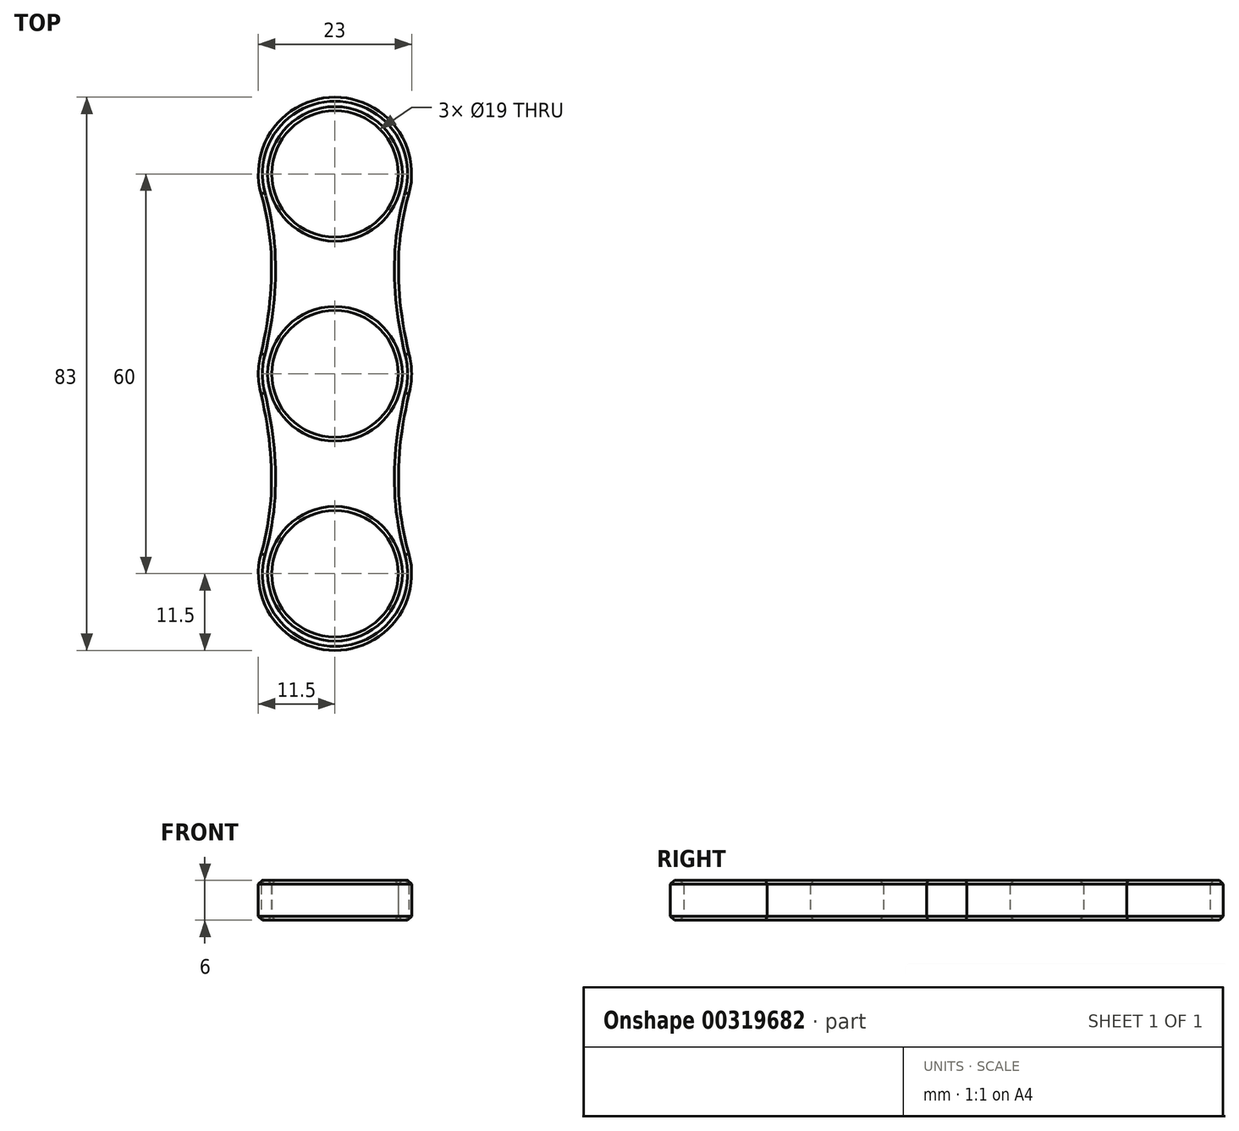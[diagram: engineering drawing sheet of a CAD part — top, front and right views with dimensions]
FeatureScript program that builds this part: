
annotation { "Feature Type Name" : "Feature", "Feature Type Description" : "" }
export const myFeature = defineFeature(function(context is Context, id is Id, definition is map)
    precondition{}
    {
        {
            var Q0;
            Q0=qCreatedBy(makeId("Top.planeOp"),FACE);
            var sketch = newSketch(context, id + "F0", { "sketchPlane" : qUnion([Q0])});
            skPoint(sketch, "E0", {"position": v(0, 30) * mm});
            skCircle(sketch, "E1", {"center": v(0, 0) * mm, "radius": 9.5 * mm});
            skCircle(sketch, "E2.0", {"center": v(0, 0) * mm, "radius": 11.5 * mm});
            skCircle(sketch, "E3", {"center": v(0, 30) * mm, "radius": 9.5 * mm});
            skCircle(sketch, "E4.0", {"center": v(0, 30) * mm, "radius": 11.5 * mm});
            skFitSpline(sketch, "E5", {"points": [v(-11.1, 27) * mm, v(-11.1, 3) * mm], "startDerivative": vector(6.3, -21) * mm, "endDerivative": vector(-6.3, -27) * mm});
            skFitSpline(sketch, "E6", {"points": [v(11.1, 27) * mm, v(11.1, 3) * mm], "startDerivative": vector(-6.3, -21) * mm, "endDerivative": vector(6.3, -27) * mm});
            skLineSegment(sketch, "E7", {"start": v(-22.96, 0) * mm, "end": v(18.82, 0) * mm, "construction": true});
            skSolve(sketch);
        }
        {
            var Q0;
            Q0=makeQuery(id+"F0.imprint","IMPRINT",FACE,{"disambiguationData":[TD([[makeQuery(id+"F0.imprint","IMPRINT",EDGE,{"derivedFrom":sQuery(id+"F0.wireOp",EDGE,"E3")}),-1.0]])]});
            var Q1;
            {var subQ0=sQuery(id+"F0.wireOp",EDGE,"E6");var subQ1=sQuery(id+"F0.wireOp",EDGE,"E2.0");var subQ2=makeQuery(id+"F0.imprint","INTERSECT",VERTEX,{"disambiguationData":[OD(1.0)],"derivedFrom":[subQ1,subQ0]});Q1=makeQuery(id+"F0.imprint","IMPRINT",FACE,{"disambiguationData":[TD([[makeQuery(id+"F0.imprint","IMPRINT",EDGE,{"disambiguationData":[TD([[subQ2,-1.0]])],"derivedFrom":subQ1}),-1.0]])]});}
            var Q2;
            Q2=makeQuery(id+"F0.imprint","IMPRINT",FACE,{"disambiguationData":[TD([[makeQuery(id+"F0.imprint","IMPRINT",EDGE,{"derivedFrom":sQuery(id+"F0.wireOp",EDGE,"E1")}),-1.0]])]});
            extrude(context, id + "F1", {"entities" : qUnion([Q0, Q1, Q2]), "depth" : 6 * mm});
        }
        {
            var Q0;
            Q0=makeQuery(id+"F1.opExtrude","SWEPT_BODY",BODY,{"disambiguationData":[OSD([sQuery(id+"F0.wireOp",EDGE,"E1"),sQuery(id+"F0.wireOp",EDGE,"E2.0"),sQuery(id+"F0.wireOp",EDGE,"E3"),sQuery(id+"F0.wireOp",EDGE,"E4.0"),sQuery(id+"F0.wireOp",EDGE,"E5"),sQuery(id+"F0.wireOp",EDGE,"E6")])]});
            var Q1;
            Q1=qCreatedBy(makeId("Front.planeOp"),FACE);
            mirror(context, id + "F2", {"operationType" : NewBodyOperationType.ADD, "entities" : qUnion([Q0]), "mirrorPlane" : qUnion([Q1])});
        }
        {
            var Q0;
            {var subQ0=makeQuery(id+"F1.opExtrude","CAP_FACE",FACE,{"disambiguationData":[OSD([sQuery(id+"F0.wireOp",EDGE,"E1"),sQuery(id+"F0.wireOp",EDGE,"E2.0"),sQuery(id+"F0.wireOp",EDGE,"E3"),sQuery(id+"F0.wireOp",EDGE,"E4.0"),sQuery(id+"F0.wireOp",EDGE,"E5"),sQuery(id+"F0.wireOp",EDGE,"E6")])],"isStart":false});Q0=makeQuery(id+"F2.boolean.opBoolean","MERGE",FACE,{"derivedFrom":[subQ0,makeQuery(id+"F2.opPattern","COPY",FACE,{"derivedFrom":subQ0,"instanceName":"1"})]});}
            var Q1;
            {var subQ0=makeQuery(id+"F1.opExtrude","CAP_FACE",FACE,{"disambiguationData":[OSD([sQuery(id+"F0.wireOp",EDGE,"E1"),sQuery(id+"F0.wireOp",EDGE,"E2.0"),sQuery(id+"F0.wireOp",EDGE,"E3"),sQuery(id+"F0.wireOp",EDGE,"E4.0"),sQuery(id+"F0.wireOp",EDGE,"E5"),sQuery(id+"F0.wireOp",EDGE,"E6")])],"isStart":true});Q1=makeQuery(id+"F2.boolean.opBoolean","MERGE",FACE,{"derivedFrom":[subQ0,makeQuery(id+"F2.opPattern","COPY",FACE,{"derivedFrom":subQ0,"instanceName":"1"})]});}
            chamfer(context, id + "F3", {"entities" : qUnion([Q0, Q1]), "width" : 0.6 * mm, "tangentPropagation" : true});
        }
    });
